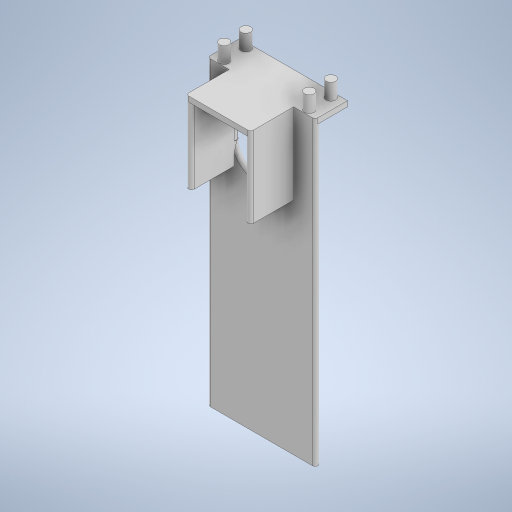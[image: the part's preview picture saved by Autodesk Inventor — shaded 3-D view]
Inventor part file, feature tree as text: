
AUTODESK INVENTOR PART (.ipt)
format: ipt  version: 2023 (Build 270158000, 158)  size: 356,864 bytes
history: native  units: mm
features: extrude x7, sketch x7, fillet x2
ambient origin geometry x8: Origin, YZ Plane, XZ Plane, XY Plane, X Axis, Y Axis, Z Axis, Center Point
bodies: Solid1 (feature_tree)
feature tree (16):
  extrude  "Extrusion1"  Depth=200.0mm
  extrude  "Extrusion6"  Depth=50.0mm
  sketch  "Sketch15"  dims[d22=50.0mm d23=20.0mm]
  sketch  "Sketch16"  dims[d24=5.0mm d25=0.0mm d46=100.0mm]
  extrude  "Extrusion11"  Depth=20.0mm
  extrude  "Extrusion12"  Depth=100.0mm
  extrude  "Extrusion17"  Depth=9.0mm
  extrude  "Extrusion18"  Depth=9.0mm
  extrude  "Extrusion19"  Depth=2.5mm TaperAngle=0.0deg
  fillet  "Fillet1"  Radius=15.0mm
  fillet  "Fillet2"  Radius=100.0mm
  sketch  "Sketch1"  dims[d0=100.0mm d1=200.0mm]
  sketch  "Sketch6"  dims[d2=5.0mm d3=0.0mm d21=50.0mm]
  sketch  "Sketch21"  dims[d47=30.0mm d48=9.0mm]
  sketch  "Sketch23"  dims[d49=9.0mm d50=9.0mm]
  sketch  "Sketch24"  dims[d51=9.0mm d52=5.0mm d53=0.0mm d54=15.0mm d55=0.0mm d66=100.0mm d67=80.0mm d68=5.0mm d69=0.0mm d72=60.0mm d73=75.0mm d74=40.0mm d75=0.0mm d76=50.0mm d77=40.0mm d78=0.0mm d79=2.5mm d80=2.5mm d81=0.0mm d82=0.0mm]
